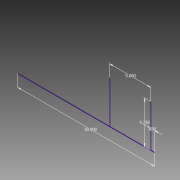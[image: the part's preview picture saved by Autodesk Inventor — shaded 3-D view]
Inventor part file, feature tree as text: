
AUTODESK INVENTOR PART (.ipt)
format: ipt  version: 2013 (Build 170138000, 138)  size: 61,952 bytes
history: native  units: in
note: dims shown in document units (in); Inventor stores cm internally (conversion verified against a paired STEP export)
features: sketch x1
ambient origin geometry x8: Origin, YZ Plane, XZ Plane, XY Plane, X Axis, Y Axis, Z Axis, Center Point
feature tree (1):
  sketch  "Sketch1"  dims[d0=30.0in d2=9.25in d3=0.83in d4=9.0in]
